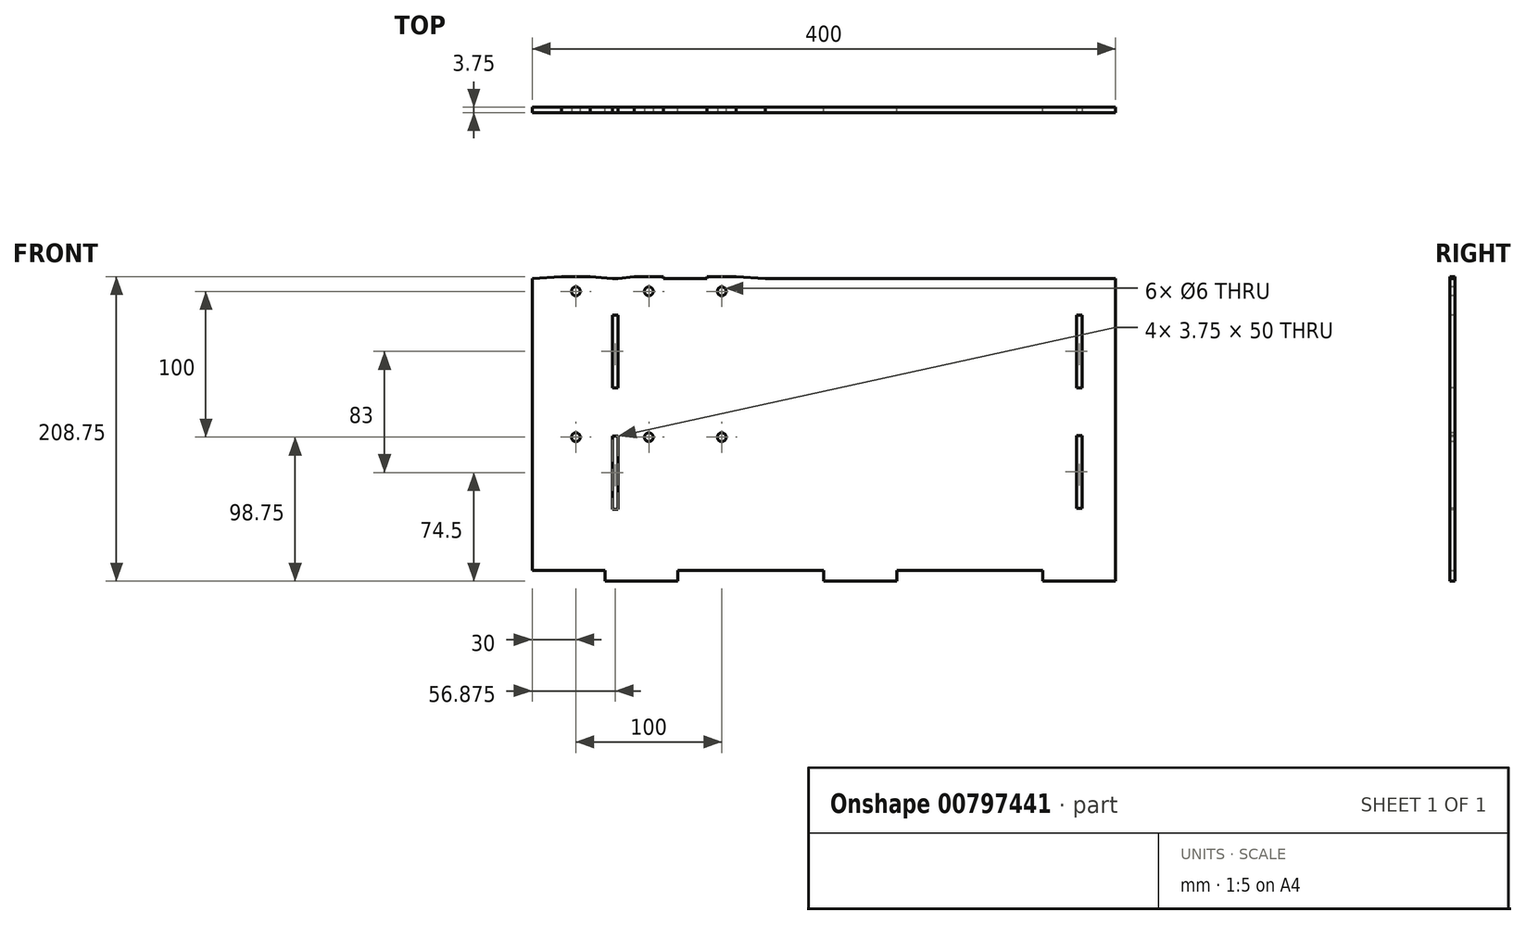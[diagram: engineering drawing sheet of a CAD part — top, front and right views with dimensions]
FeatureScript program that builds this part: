
annotation { "Feature Type Name" : "Feature", "Feature Type Description" : "" }
export const myFeature = defineFeature(function(context is Context, id is Id, definition is map)
    precondition{}
    {
        {
            var Q0;
            Q0=qCreatedBy(makeId("Front.planeOp"),FACE);
            var sketch = newSketch(context, id + "F0", { "sketchPlane" : qUnion([Q0])});
            skLineSegment(sketch, "E0.bottom", {"start": v(50, 0) * mm, "end": v(150, 0) * mm});
            skLineSegment(sketch, "E0.top", {"start": v(0, 200) * mm, "end": v(350, 200) * mm});
            skLineSegment(sketch, "E0.right", {"start": v(350, 0) * mm, "end": v(350, 200) * mm});
            skLineSegment(sketch, "E1.top", {"start": v(0, -7.5) * mm, "end": v(50, -7.5) * mm});
            skLineSegment(sketch, "E1.left", {"start": v(0, 0) * mm, "end": v(0, -7.5) * mm});
            skLineSegment(sketch, "E1.right", {"start": v(50, 0) * mm, "end": v(50, -7.5) * mm});
            skLineSegment(sketch, "E2.top", {"start": v(350, -7.5) * mm, "end": v(300, -7.5) * mm});
            skLineSegment(sketch, "E2.left", {"start": v(350, 0) * mm, "end": v(350, -7.5) * mm});
            skLineSegment(sketch, "E2.right", {"start": v(300, 0) * mm, "end": v(300, -7.5) * mm});
            skLineSegment(sketch, "E3.top", {"start": v(150, -7.5) * mm, "end": v(200, -7.5) * mm});
            skLineSegment(sketch, "E3.left", {"start": v(150, 0) * mm, "end": v(150, -7.5) * mm});
            skLineSegment(sketch, "E3.right", {"start": v(200, 0) * mm, "end": v(200, -7.5) * mm});
            skLineSegment(sketch, "E4.trimOffspring", {"start": v(200, 0) * mm, "end": v(300, 0) * mm});
            skLineSegment(sketch, "E5.bottom", {"start": v(0, 200) * mm, "end": v(-50, 200) * mm});
            skLineSegment(sketch, "E5.top", {"start": v(0, 0) * mm, "end": v(-50, 0) * mm});
            skLineSegment(sketch, "E5.right", {"start": v(-50, 200) * mm, "end": v(-50, 0) * mm});
            skSolve(sketch);
        }
        {
            var Q0;
            Q0=makeQuery(id+"F0.imprint","IMPRINT",FACE,{"disambiguationData":[TD([[makeQuery(id+"F0.imprint","IMPRINT",EDGE,{"derivedFrom":sQuery(id+"F0.wireOp",EDGE,"E0.bottom")}),1.0]])]});
            extrude(context, id + "F1", {"entities" : qUnion([Q0]), "depth" : 3.75 * mm, "offsetDistance" : 25 * mm});
        }
        {
            var Q0;
            Q0=makeQuery(id+"F1.opExtrude","CAP_FACE",FACE,{"disambiguationData":[OSD([sQuery(id+"F0.wireOp",EDGE,"E0.bottom"),sQuery(id+"F0.wireOp",EDGE,"E0.top"),sQuery(id+"F0.wireOp",EDGE,"E0.left"),sQuery(id+"F0.wireOp",EDGE,"E0.right"),sQuery(id+"F0.wireOp",EDGE,"E1.top"),sQuery(id+"F0.wireOp",EDGE,"E1.left"),sQuery(id+"F0.wireOp",EDGE,"E1.right"),sQuery(id+"F0.wireOp",EDGE,"E2.top"),sQuery(id+"F0.wireOp",EDGE,"E2.left"),sQuery(id+"F0.wireOp",EDGE,"E2.right")])],"isStart":false});
            var sketch = newSketch(context, id + "F2", { "sketchPlane" : qUnion([Q0])});
            skLineSegment(sketch, "E6.bottom", {"start": v(323.13, 92.5) * mm, "end": v(326.88, 92.5) * mm});
            skLineSegment(sketch, "E6.top", {"start": v(323.13, 42.5) * mm, "end": v(326.88, 42.5) * mm});
            skLineSegment(sketch, "E6.left", {"start": v(323.13, 92.5) * mm, "end": v(323.13, 42.5) * mm});
            skLineSegment(sketch, "E6.right", {"start": v(326.88, 92.5) * mm, "end": v(326.88, 42.5) * mm});
            skLineSegment(sketch, "E7.bottom", {"start": v(326.88, 175) * mm, "end": v(323.13, 175) * mm});
            skLineSegment(sketch, "E7.top", {"start": v(326.88, 125) * mm, "end": v(323.13, 125) * mm});
            skLineSegment(sketch, "E7.left", {"start": v(326.88, 175) * mm, "end": v(326.88, 125) * mm});
            skLineSegment(sketch, "E7.right", {"start": v(323.13, 175) * mm, "end": v(323.13, 125) * mm});
            skSolve(sketch);
        }
        {
            var Q0;
            Q0=makeQuery(id+"F2.imprint","IMPRINT",FACE,{"disambiguationData":[TD([[makeQuery(id+"F2.imprint","IMPRINT",EDGE,{"derivedFrom":sQuery(id+"F2.wireOp",EDGE,"E7.bottom")}),1.0]])]});
            var Q1;
            Q1=makeQuery(id+"F2.imprint","IMPRINT",FACE,{"disambiguationData":[TD([[makeQuery(id+"F2.imprint","IMPRINT",EDGE,{"derivedFrom":sQuery(id+"F2.wireOp",EDGE,"E6.bottom")}),-1.0]])]});
            extrude(context, id + "F3", {"entities" : qUnion([Q0, Q1]), "operationType" : NewBodyOperationType.REMOVE, "oppositeDirection" : true, "depth" : 3.75 * mm, "offsetDistance" : 25 * mm});
        }
        {
            var Q0;
            Q0=makeQuery(id+"F1.opExtrude","SWEPT_FACE",FACE,{"disambiguationData":[OSD([sQuery(id+"F0.wireOp",EDGE,"E0.top")])]});
            var sketch = newSketch(context, id + "F4", { "sketchPlane" : qUnion([Q0])});
            skLineSegment(sketch, "E8.bottom", {"start": v(70, 0) * mm, "end": v(90, 0) * mm});
            skLineSegment(sketch, "E8.top", {"start": v(70, -3.75) * mm, "end": v(90, -3.75) * mm});
            skLineSegment(sketch, "E8.left", {"start": v(90, 0) * mm, "end": v(90, -3.75) * mm});
            skLineSegment(sketch, "E8.right", {"start": v(70, 0) * mm, "end": v(70, -3.75) * mm});
            skLineSegment(sketch, "E9.bottom", {"start": v(40, -3.75) * mm, "end": v(20, -3.75) * mm});
            skLineSegment(sketch, "E9.top", {"start": v(40, 0) * mm, "end": v(20, 0) * mm});
            skLineSegment(sketch, "E9.left", {"start": v(40, -3.75) * mm, "end": v(40, 0) * mm});
            skLineSegment(sketch, "E9.right", {"start": v(20, -3.75) * mm, "end": v(20, 0) * mm});
            skLineSegment(sketch, "E10.bottom", {"start": v(-10, -3.75) * mm, "end": v(-30, -3.75) * mm});
            skLineSegment(sketch, "E10.top", {"start": v(-10, 0) * mm, "end": v(-30, 0) * mm});
            skLineSegment(sketch, "E10.left", {"start": v(-10, -3.75) * mm, "end": v(-10, 0) * mm});
            skLineSegment(sketch, "E10.right", {"start": v(-30, -3.75) * mm, "end": v(-30, 0) * mm});
            skSolve(sketch);
        }
        {
            var Q0;
            Q0=makeQuery(id+"F4.imprint","IMPRINT",FACE,{"disambiguationData":[TD([[makeQuery(id+"F4.imprint","IMPRINT",EDGE,{"derivedFrom":sQuery(id+"F4.wireOp",EDGE,"E8.bottom")}),-1.0]])]});
            var Q1;
            Q1=makeQuery(id+"F4.imprint","IMPRINT",FACE,{"disambiguationData":[TD([[makeQuery(id+"F4.imprint","IMPRINT",EDGE,{"derivedFrom":sQuery(id+"F4.wireOp",EDGE,"E9.bottom")}),1.0]])]});
            var Q2;
            Q2=makeQuery(id+"F4.imprint","IMPRINT",FACE,{"disambiguationData":[TD([[makeQuery(id+"F4.imprint","IMPRINT",EDGE,{"derivedFrom":sQuery(id+"F4.wireOp",EDGE,"E10.bottom")}),1.0]])]});
            extrude(context, id + "F5", {"entities" : qUnion([Q0, Q1, Q2]), "operationType" : NewBodyOperationType.ADD, "depth" : 1.25 * mm, "offsetDistance" : 25 * mm});
        }
        {
            var Q0;
            Q0=makeQuery(id+"F1.opExtrude","CAP_FACE",FACE,{"disambiguationData":[OSD([sQuery(id+"F0.wireOp",EDGE,"E0.bottom"),sQuery(id+"F0.wireOp",EDGE,"E0.top"),sQuery(id+"F0.wireOp",EDGE,"E0.left"),sQuery(id+"F0.wireOp",EDGE,"E0.right"),sQuery(id+"F0.wireOp",EDGE,"E1.top"),sQuery(id+"F0.wireOp",EDGE,"E1.left"),sQuery(id+"F0.wireOp",EDGE,"E1.right"),sQuery(id+"F0.wireOp",EDGE,"E2.top"),sQuery(id+"F0.wireOp",EDGE,"E2.left"),sQuery(id+"F0.wireOp",EDGE,"E2.right")])],"isStart":true});
            var sketch = newSketch(context, id + "F6", { "sketchPlane" : qUnion([Q0])});
            skLineSegment(sketch, "E11", {"start": v(-350, 0) * mm, "end": v(0, 0) * mm});
            skPoint(sketch, "E12", {"position": v(-80, 91.25) * mm});
            skPoint(sketch, "E13", {"position": v(-80, 191.25) * mm});
            skPoint(sketch, "E14", {"position": v(-30, 91.25) * mm});
            skPoint(sketch, "E15", {"position": v(-30, 191.25) * mm});
            skPoint(sketch, "E16", {"position": v(20, 191.25) * mm});
            skPoint(sketch, "E17", {"position": v(20, 91.25) * mm});
            skLineSegment(sketch, "E18", {"start": v(-80, 191.25) * mm, "end": v(20, 91.25) * mm});
            skLineSegment(sketch, "E19", {"start": v(20, 191.25) * mm, "end": v(-80, 91.25) * mm});
            skPoint(sketch, "E20", {"position": v(-30, 141.25) * mm});
            skSolve(sketch);
        }
        {
            var Q0;
            Q0=sQuery(id+"F6.wireOp",VERTEX,"E12");
            var Q1;
            Q1=sQuery(id+"F6.wireOp",VERTEX,"E13");
            var Q2;
            Q2=sQuery(id+"F6.wireOp",VERTEX,"E14");
            var Q3;
            Q3=sQuery(id+"F6.wireOp",VERTEX,"E17");
            var Q4;
            Q4=sQuery(id+"F6.wireOp",VERTEX,"E16");
            var Q5;
            Q5=sQuery(id+"F6.wireOp",VERTEX,"E15");
            var Q6;
            Q6=makeQuery(id+"F1.opExtrude","SWEPT_BODY",BODY,{"disambiguationData":[OSD([sQuery(id+"F0.wireOp",EDGE,"E0.bottom"),sQuery(id+"F0.wireOp",EDGE,"E0.top"),sQuery(id+"F0.wireOp",EDGE,"E0.left"),sQuery(id+"F0.wireOp",EDGE,"E0.right"),sQuery(id+"F0.wireOp",EDGE,"E1.top"),sQuery(id+"F0.wireOp",EDGE,"E1.left"),sQuery(id+"F0.wireOp",EDGE,"E1.right"),sQuery(id+"F0.wireOp",EDGE,"E2.top"),sQuery(id+"F0.wireOp",EDGE,"E2.left"),sQuery(id+"F0.wireOp",EDGE,"E2.right")])]});
            hole(context, id + "F7", {"style" : HoleStyle.SIMPLE, "endStyle" : HoleEndStyle.BLIND, "holeDiameter" : 6 * mm, "majorDiameter" : 5 * mm, "holeDepth" : 4 * mm, "isTappedThrough" : true, "tappedDepth" : 12 * mm, "tapClearance" : 3, "locations" : qUnion([Q0, Q1, Q2, Q3, Q4, Q5]), "scope" : qUnion([Q6])});
        }
        {
            var Q0;
            Q0=makeQuery(id+"F5.boolean.opBoolean","MERGE",FACE,{"derivedFrom":[makeQuery(id+"F1.opExtrude","CAP_FACE",FACE,{"disambiguationData":[OSD([sQuery(id+"F0.wireOp",EDGE,"E0.bottom"),sQuery(id+"F0.wireOp",EDGE,"E0.top"),sQuery(id+"F0.wireOp",EDGE,"E0.right"),sQuery(id+"F0.wireOp",EDGE,"E1.top"),sQuery(id+"F0.wireOp",EDGE,"E1.left"),sQuery(id+"F0.wireOp",EDGE,"E1.right"),sQuery(id+"F0.wireOp",EDGE,"E2.top"),sQuery(id+"F0.wireOp",EDGE,"E2.left"),sQuery(id+"F0.wireOp",EDGE,"E2.right"),sQuery(id+"F0.wireOp",EDGE,"E3.top"),sQuery(id+"F0.wireOp",EDGE,"E3.left"),sQuery(id+"F0.wireOp",EDGE,"E3.right"),sQuery(id+"F0.wireOp",EDGE,"E4.trimOffspring"),sQuery(id+"F0.wireOp",EDGE,"E5.bottom"),sQuery(id+"F0.wireOp",EDGE,"E5.top"),sQuery(id+"F0.wireOp",EDGE,"E5.right")])],"isStart":true}),makeQuery(id+"F5.opExtrude","SWEPT_FACE",FACE,{"disambiguationData":[OSD([sQuery(id+"F4.wireOp",EDGE,"E8.bottom")])]}),makeQuery(id+"F5.opExtrude","SWEPT_FACE",FACE,{"disambiguationData":[OSD([sQuery(id+"F4.wireOp",EDGE,"E9.top")])]}),makeQuery(id+"F5.opExtrude","SWEPT_FACE",FACE,{"disambiguationData":[OSD([sQuery(id+"F4.wireOp",EDGE,"E10.top")])]})]});
            var sketch = newSketch(context, id + "F8", { "sketchPlane" : qUnion([Q0])});
            skLineSegment(sketch, "E21.bottom", {"start": v(-90, 201.25) * mm, "end": v(-20, 201.25) * mm});
            skLineSegment(sketch, "E21.top", {"start": v(-90, 200) * mm, "end": v(30, 200) * mm});
            skLineSegment(sketch, "E21.left", {"start": v(-90, 201.25) * mm, "end": v(-90, 200) * mm});
            skLineSegment(sketch, "E21.right", {"start": v(30, 201.25) * mm, "end": v(30, 200) * mm});
            skLineSegment(sketch, "E22", {"start": v(30, 201.25) * mm, "end": v(50, 200) * mm});
            skLineSegment(sketch, "E23", {"start": v(-90, 201.25) * mm, "end": v(-110, 200) * mm});
            skLineSegment(sketch, "E24.bottom", {"start": v(-70, 201.25) * mm, "end": v(-40, 201.25) * mm});
            skLineSegment(sketch, "E24.top", {"start": v(-70, 200) * mm, "end": v(-40, 200) * mm});
            skLineSegment(sketch, "E24.left", {"start": v(-70, 201.25) * mm, "end": v(-70, 200) * mm});
            skLineSegment(sketch, "E24.right", {"start": v(-40, 201.25) * mm, "end": v(-40, 200) * mm});
            skLineSegment(sketch, "E25.top", {"start": v(-20, 200) * mm, "end": v(10, 200) * mm});
            skLineSegment(sketch, "E25.left", {"start": v(-20, 201.25) * mm, "end": v(-20, 200) * mm});
            skLineSegment(sketch, "E25.right", {"start": v(10, 201.25) * mm, "end": v(10, 200) * mm});
            skLineSegment(sketch, "E26.top", {"start": v(-8.75, 200) * mm, "end": v(-5, 200) * mm});
            skLineSegment(sketch, "E27", {"start": v(10, 201.25) * mm, "end": v(-5, 200) * mm});
            skLineSegment(sketch, "E28", {"start": v(-8.75, 200) * mm, "end": v(-20, 201.25) * mm});
            skLineSegment(sketch, "E29.trimOffspring", {"start": v(10, 201.25) * mm, "end": v(30, 201.25) * mm});
            skSolve(sketch);
        }
        {
            var Q0;
            Q0=makeQuery(id+"F8.imprint","IMPRINT",FACE,{"disambiguationData":[TD([[makeQuery(id+"F8.imprint","IMPRINT",EDGE,{"derivedFrom":sQuery(id+"F8.wireOp",EDGE,"E24.bottom")}),-1.0]])]});
            var Q1;
            Q1=makeQuery(id+"F8.imprint","IMPRINT",FACE,{"disambiguationData":[TD([[makeQuery(id+"F8.imprint","IMPRINT",EDGE,{"derivedFrom":sQuery(id+"F8.wireOp",EDGE,"E25.bottom")}),-1.0]])]});
            var Q2;
            Q2=makeQuery(id+"F8.imprint","IMPRINT",FACE,{"disambiguationData":[TD([[makeQuery(id+"F8.imprint","IMPRINT",EDGE,{"derivedFrom":sQuery(id+"F8.wireOp",EDGE,"E21.right")}),1.0]])]});
            var Q3;
            {var subQ0=sQuery(id+"F8.wireOp",EDGE,"E21.left");Q3=makeQuery(id+"F8.imprint","IMPRINT",FACE,{"disambiguationData":[TD([[makeQuery(id+"F8.imprint","IMPRINT",EDGE,{"derivedFrom":subQ0}),-1.0]])]});}
            var Q4;
            {var subQ0=sQuery(id+"F8.wireOp",EDGE,"E25.right");Q4=makeQuery(id+"F8.imprint","IMPRINT",FACE,{"disambiguationData":[TD([[makeQuery(id+"F8.imprint","IMPRINT",EDGE,{"derivedFrom":subQ0}),-1.0]])]});}
            var Q5;
            {var subQ0=sQuery(id+"F8.wireOp",EDGE,"E25.left");Q5=makeQuery(id+"F8.imprint","IMPRINT",FACE,{"disambiguationData":[TD([[makeQuery(id+"F8.imprint","IMPRINT",EDGE,{"derivedFrom":subQ0}),1.0]])]});}
            extrude(context, id + "F9", {"entities" : qUnion([Q0, Q1, Q2, Q3, Q4, Q5]), "operationType" : NewBodyOperationType.ADD, "oppositeDirection" : true, "depth" : 3.75 * mm, "offsetDistance" : 25 * mm});
        }
        {
            var Q0;
            {var subQ0=sQuery(id+"F0.wireOp",EDGE,"E5.bottom");var subQ1=sQuery(id+"F0.wireOp",EDGE,"E0.top");Q0=makeQuery(id+"F9.boolean.opBoolean","MERGE",FACE,{"derivedFrom":[makeQuery(id+"F5.boolean.opBoolean","MERGE",FACE,{"derivedFrom":[makeQuery(id+"F1.opExtrude","CAP_FACE",FACE,{"disambiguationData":[OSD([sQuery(id+"F0.wireOp",EDGE,"E0.bottom"),subQ1,sQuery(id+"F0.wireOp",EDGE,"E0.right"),sQuery(id+"F0.wireOp",EDGE,"E1.top"),sQuery(id+"F0.wireOp",EDGE,"E1.left"),sQuery(id+"F0.wireOp",EDGE,"E1.right"),sQuery(id+"F0.wireOp",EDGE,"E2.top"),sQuery(id+"F0.wireOp",EDGE,"E2.left"),sQuery(id+"F0.wireOp",EDGE,"E2.right"),sQuery(id+"F0.wireOp",EDGE,"E3.top"),sQuery(id+"F0.wireOp",EDGE,"E3.left"),sQuery(id+"F0.wireOp",EDGE,"E3.right"),sQuery(id+"F0.wireOp",EDGE,"E4.trimOffspring"),subQ0,sQuery(id+"F0.wireOp",EDGE,"E5.top"),sQuery(id+"F0.wireOp",EDGE,"E5.right")])],"isStart":true}),makeQuery(id+"F5.opExtrude","SWEPT_FACE",FACE,{"disambiguationData":[OSD([sQuery(id+"F4.wireOp",EDGE,"E8.bottom")])]}),makeQuery(id+"F5.opExtrude","SWEPT_FACE",FACE,{"disambiguationData":[OSD([sQuery(id+"F4.wireOp",EDGE,"E9.top")])]}),makeQuery(id+"F5.opExtrude","SWEPT_FACE",FACE,{"disambiguationData":[OSD([sQuery(id+"F4.wireOp",EDGE,"E10.top")])]})]}),makeQuery(id+"F9.opExtrude","CAP_FACE",FACE,{"disambiguationData":[OSD([subQ1,subQ0,sQuery(id+"F8.wireOp",EDGE,"E21.left"),sQuery(id+"F8.wireOp",EDGE,"E23")])],"isStart":true}),makeQuery(id+"F9.opExtrude","CAP_FACE",FACE,{"disambiguationData":[OSD([subQ1,subQ0,sQuery(id+"F8.wireOp",EDGE,"E21.right"),sQuery(id+"F8.wireOp",EDGE,"E22")])],"isStart":true}),makeQuery(id+"F9.opExtrude","CAP_FACE",FACE,{"disambiguationData":[OSD([sQuery(id+"F8.wireOp",EDGE,"E24.bottom"),sQuery(id+"F8.wireOp",EDGE,"E24.top"),sQuery(id+"F8.wireOp",EDGE,"E24.left"),sQuery(id+"F8.wireOp",EDGE,"E24.right")])],"isStart":true}),makeQuery(id+"F9.opExtrude","CAP_FACE",FACE,{"disambiguationData":[OSD([sQuery(id+"F8.wireOp",EDGE,"E25.bottom"),sQuery(id+"F8.wireOp",EDGE,"E25.top"),sQuery(id+"F8.wireOp",EDGE,"E25.left"),sQuery(id+"F8.wireOp",EDGE,"E25.right")])],"isStart":true})]});}
            var sketch = newSketch(context, id + "F10", { "sketchPlane" : qUnion([Q0])});
            skLineSegment(sketch, "E30.bottom", {"start": v(-8.75, 92) * mm, "end": v(-5, 92) * mm});
            skLineSegment(sketch, "E30.top", {"start": v(-8.75, 42) * mm, "end": v(-5, 42) * mm});
            skLineSegment(sketch, "E30.left", {"start": v(-8.75, 92) * mm, "end": v(-8.75, 42) * mm});
            skLineSegment(sketch, "E30.right", {"start": v(-5, 92) * mm, "end": v(-5, 42) * mm});
            skLineSegment(sketch, "E31.bottom", {"start": v(-5, 175) * mm, "end": v(-8.75, 175) * mm});
            skLineSegment(sketch, "E31.top", {"start": v(-5, 125) * mm, "end": v(-8.75, 125) * mm});
            skLineSegment(sketch, "E31.left", {"start": v(-5, 175) * mm, "end": v(-5, 125) * mm});
            skLineSegment(sketch, "E31.right", {"start": v(-8.75, 175) * mm, "end": v(-8.75, 125) * mm});
            skSolve(sketch);
        }
        {
            var Q0;
            Q0=makeQuery(id+"F10.imprint","IMPRINT",FACE,{"disambiguationData":[TD([[makeQuery(id+"F10.imprint","IMPRINT",EDGE,{"derivedFrom":sQuery(id+"F10.wireOp",EDGE,"E31.bottom")}),1.0]])]});
            var Q1;
            Q1=makeQuery(id+"F10.imprint","IMPRINT",FACE,{"disambiguationData":[TD([[makeQuery(id+"F10.imprint","IMPRINT",EDGE,{"derivedFrom":sQuery(id+"F10.wireOp",EDGE,"E30.bottom")}),-1.0]])]});
            extrude(context, id + "F11", {"entities" : qUnion([Q0, Q1]), "operationType" : NewBodyOperationType.REMOVE, "oppositeDirection" : true, "depth" : 3.75 * mm, "offsetDistance" : 25 * mm});
        }
    });
